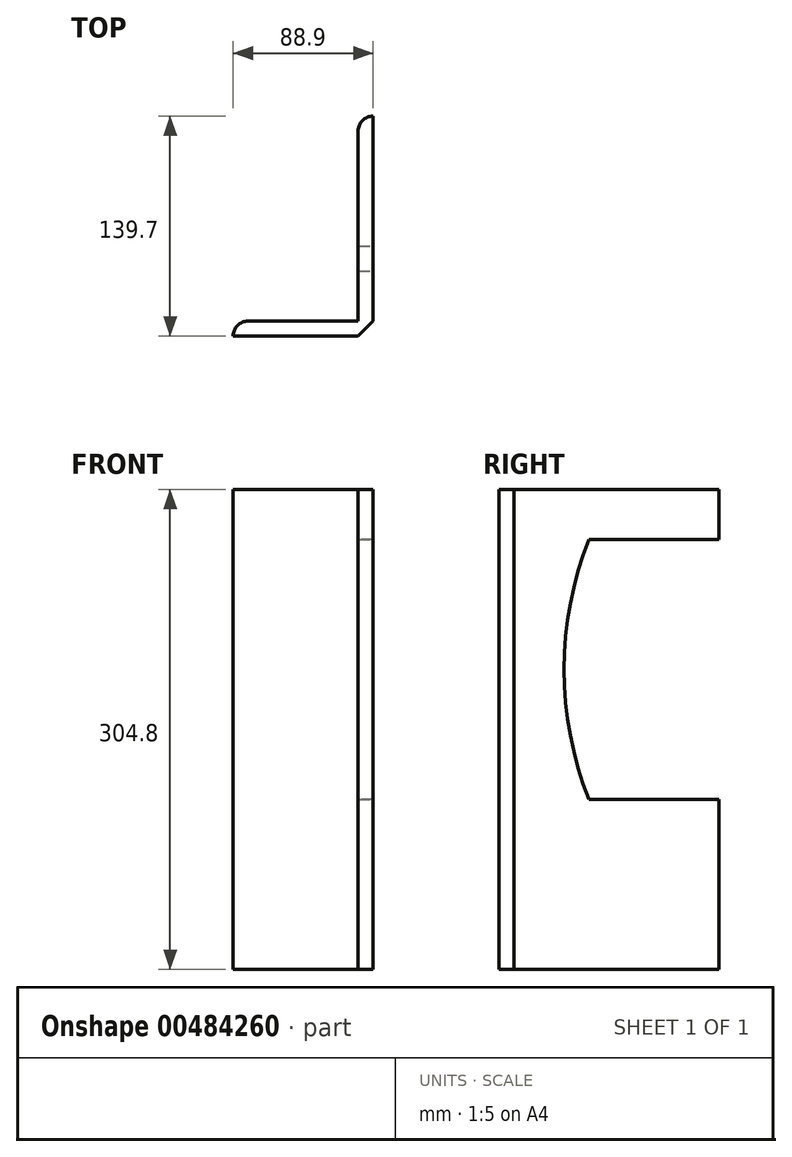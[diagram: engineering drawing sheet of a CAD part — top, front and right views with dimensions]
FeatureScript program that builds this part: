
annotation { "Feature Type Name" : "Feature", "Feature Type Description" : "" }
export const myFeature = defineFeature(function(context is Context, id is Id, definition is map)
    precondition{}
    {
        {
            var Q0;
            Q0=qCreatedBy(makeId("Top.planeOp"),FACE);
            var sketch = newSketch(context, id + "F0", { "sketchPlane" : qUnion([Q0])});
            skLineSegment(sketch, "E0.bottom", {"start": v(44.45, 69.85) * mm, "end": v(44.45, 69.85) * mm});
            skLineSegment(sketch, "E0.top", {"start": v(34.92, -69.85) * mm, "end": v(-44.45, -69.85) * mm});
            skLineSegment(sketch, "E0.left", {"start": v(44.45, 69.85) * mm, "end": v(44.45, -60.33) * mm});
            skLineSegment(sketch, "E0.right", {"start": v(-44.45, -69.85) * mm, "end": v(-44.45, -69.85) * mm});
            skPoint(sketch, "E0.middle", {"position": v(0, 0) * mm});
            skPoint(sketch, "E1", {"position": v(34.93, 69.85) * mm});
            skPoint(sketch, "E2", {"position": v(-44.45, -60.33) * mm});
            skLineSegment(sketch, "E3", {"start": v(-34.93, -60.33) * mm, "end": v(34.93, -60.32) * mm});
            skLineSegment(sketch, "E4", {"start": v(34.93, 60.33) * mm, "end": v(34.93, -60.32) * mm});
            skPoint(sketch, "E5", {"position": v(34.92, -69.85) * mm});
            skPoint(sketch, "E6", {"position": v(44.45, -60.33) * mm});
            skLineSegment(sketch, "E7", {"start": v(34.92, -69.85) * mm, "end": v(44.45, -60.33) * mm});
            skPoint(sketch, "E8.orphan", {"position": v(-44.45, 69.85) * mm});
            skArc(sketch, "E9.filletArc", {"start": v(44.45, 69.85) * mm, "mid": v(37.71, 67.06) * mm, "end": v(34.93, 60.33) * mm});
            skArc(sketch, "E10.filletArc", {"start": v(-34.93, -60.33) * mm, "mid": v(-41.66, -63.11) * mm, "end": v(-44.45, -69.85) * mm});
            skPoint(sketch, "E11.orphan", {"position": v(44.45, -69.85) * mm});
            skSolve(sketch);
        }
        {
            var Q0;
            Q0=makeQuery(id+"F0.imprint","IMPRINT",FACE,{"disambiguationData":[TD([[makeQuery(id+"F0.imprint","IMPRINT",EDGE,{"derivedFrom":sQuery(id+"F0.wireOp",EDGE,"E0.top")}),-1.0]])]});
            extrude(context, id + "F1", {"entities" : qUnion([Q0]), "depth" : 304.8 * mm});
        }
        {
            var Q0;
            Q0=makeQuery(id+"F1.opExtrude","SWEPT_FACE",FACE,{"disambiguationData":[OSD([sQuery(id+"F0.wireOp",EDGE,"E0.left")])]});
            var sketch = newSketch(context, id + "F2", { "sketchPlane" : qUnion([Q0])});
            skLineSegment(sketch, "E12.bottom", {"start": v(69.85, 273.05) * mm, "end": v(-12.7, 273.05) * mm});
            skLineSegment(sketch, "E12.top", {"start": v(69.85, 107.95) * mm, "end": v(-12.7, 107.95) * mm});
            skLineSegment(sketch, "E12.left", {"start": v(69.85, 273.05) * mm, "end": v(69.85, 107.95) * mm});
            skArc(sketch, "E13", {"start": v(-12.7, 273.05) * mm, "mid": v(-28.58, 190.5) * mm, "end": v(-12.7, 107.95) * mm});
            skSolve(sketch);
        }
        {
            var Q0;
            Q0=makeQuery(id+"F2.imprint","IMPRINT",FACE,{"disambiguationData":[TD([[makeQuery(id+"F2.imprint","IMPRINT",EDGE,{"derivedFrom":sQuery(id+"F2.wireOp",EDGE,"E12.bottom")}),1.0]])]});
            extrude(context, id + "F3", {"entities" : qUnion([Q0]), "operationType" : NewBodyOperationType.REMOVE, "endBound" : BoundingType.THROUGH_ALL, "oppositeDirection" : true, "depth" : 25.4 * mm});
        }
    });
